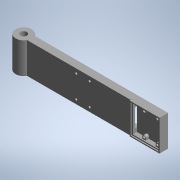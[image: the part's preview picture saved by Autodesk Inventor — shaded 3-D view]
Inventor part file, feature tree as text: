
AUTODESK INVENTOR PART (.ipt)
format: ipt  version: 2020 (Build 240168000, 168)  size: 383,488 bytes
history: native  units: mm
features: extrude x8, sketch x8, projected_geometry x6, fillet x2, chamfer x1, hole x1
ambient origin geometry x8: Origin, YZ Plane, XZ Plane, XY Plane, X Axis, Y Axis, Z Axis, Center Point
bodies: Solid1 (feature_tree)
feature tree (26):
  extrude  "Extrusion1"  Depth=6.0mm
  extrude  "Extrusion2"  Depth=7.0mm
  extrude  "Extrusion3"  Depth=28.0mm
  extrude  "Extrusion4"  Depth=7.5mm
  extrude  "Extrusion5"  Depth=25.0mm
  extrude  "Extrusion6"  Depth=21.0mm
  fillet  "Fillet3"  Radius=12.5mm
  fillet  "Fillet4"  Radius=2.0mm
  extrude  "Extrusion10"  Depth=1.6mm
  chamfer  "Chamfer1"  Distance=5.0mm
  hole  "Hole1"  [1 undecoded]
  extrude  "Extrusion11"  Depth=27.0mm
  sketch  "Sketch2"  dims[d1=13.0mm d2=6.0mm]
  sketch  "Sketch3"  dims[d3=15.0mm d5=7.0mm]
  projected_geometry  "Projected Loop1"
  sketch  "Sketch4"  dims[d6=28.0mm d7=100.0mm]
  projected_geometry  "Projected Loop2"
  sketch  "Sketch5"  dims[d8=8.0mm d10=7.5mm]
  projected_geometry  "Projected Loop3"
  sketch  "Sketch6"  dims[d11=29.0mm d12=0.0mm d13=25.0mm]
  sketch  "Sketch10"  dims[d14=24.0mm d15=21.0mm d16=12.5mm d17=2.0mm]
  projected_geometry  "Projected Loop6"
  sketch  "Sketch11"  dims[d18=4.0mm d19=1.6mm]
  projected_geometry  "Projected Loop7"
  sketch  "Sketch14"  dims[d20=1.6mm d21=5.0mm d22=0.0mm d23=26.0mm d24=27.0mm d25=1.0mm d26=0.0mm d27=2.0mm d28=0.0mm d29=0.0mm d30=17.0mm d31=26.0mm d32=0.2mm d33=2.5mm d34=0.0mm d36=92.0mm d37=19.5mm d38=0.5mm d39=0.0mm d52=25.0mm d53=5.0mm d54=5.0mm d55=8.0mm d56=2.5mm d57=0.0mm d58=10.0mm d59=2.5mm d60=45.0deg d61=2.0mm d62=12.0mm d63=4.0mm d64=2.0mm d65=90.0deg d66=17.1mm d67=20.594885mm d68=21.0mm d69=12.5mm d71=50.0mm d72=1.0mm d73=0.0mm]
  projected_geometry  "Projected Loop8"
note: 1 required parameter value undecoded (feature->parameter linkage not recoverable at this tier; creation-order binding heuristic only, values carry confidence <= 0.55)
